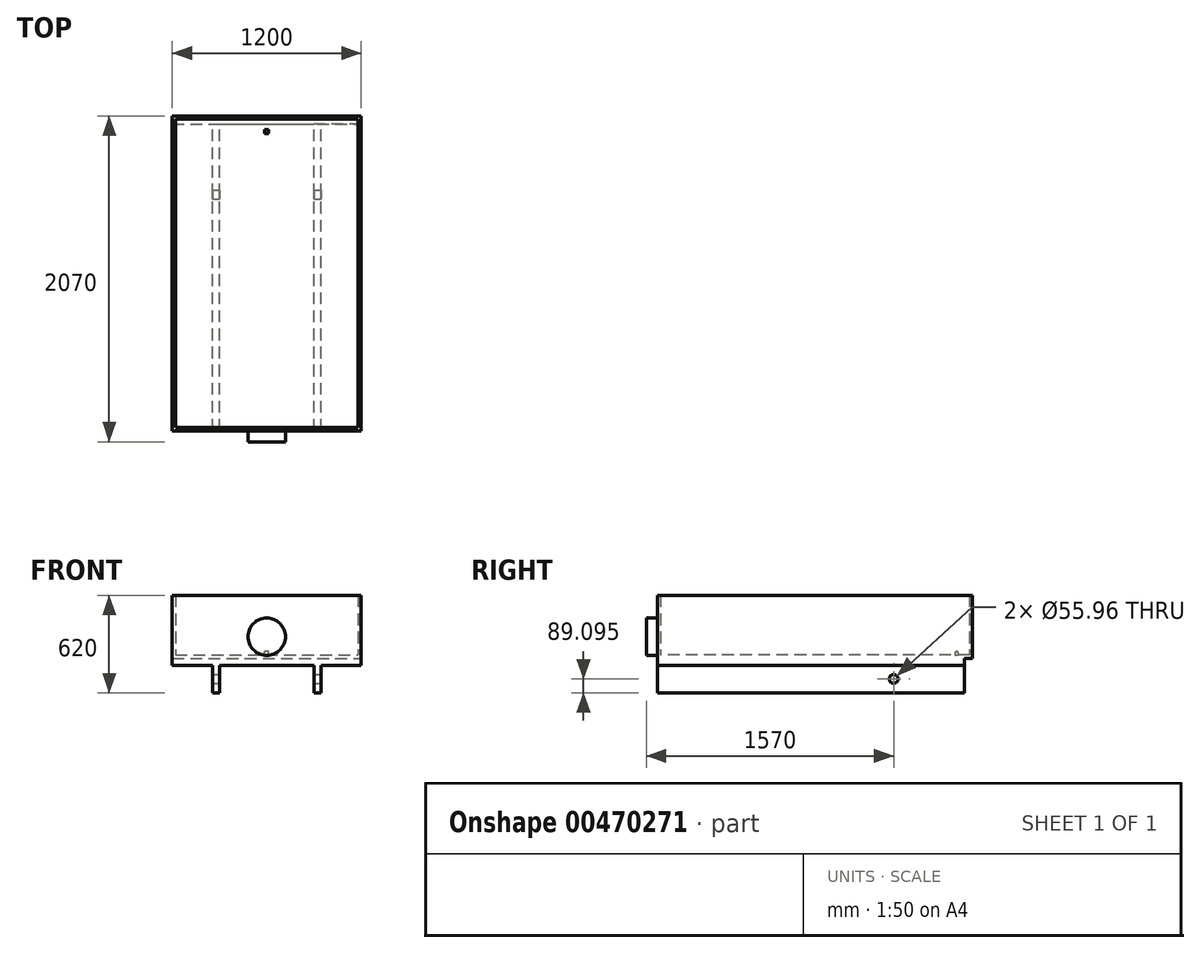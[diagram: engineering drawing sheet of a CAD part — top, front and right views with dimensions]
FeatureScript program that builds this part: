
annotation { "Feature Type Name" : "Feature", "Feature Type Description" : "" }
export const myFeature = defineFeature(function(context is Context, id is Id, definition is map)
    precondition{}
    {
        {
            var Q0;
            Q0=qCreatedBy(makeId("Top.planeOp"),FACE);
            var sketch = newSketch(context, id + "F0", { "sketchPlane" : qUnion([Q0])});
            skLineSegment(sketch, "E0.bottom", {"start": v(-600, 1000) * mm, "end": v(0, 1000) * mm});
            skLineSegment(sketch, "E0.top", {"start": v(-600, -1000) * mm, "end": v(0, -1000) * mm});
            skLineSegment(sketch, "E0.left", {"start": v(-600, 1000) * mm, "end": v(-600, -1000) * mm});
            skLineSegment(sketch, "E0.right", {"start": v(0, 1000) * mm, "end": v(0, -1000) * mm});
            skSolve(sketch);
        }
        {
            var Q0;
            Q0=makeQuery(id+"F0.imprint","IMPRINT",FACE,{"disambiguationData":[TD([[makeQuery(id+"F0.imprint","IMPRINT",EDGE,{"derivedFrom":sQuery(id+"F0.wireOp",EDGE,"E0.bottom")}),-1.0]])]});
            extrude(context, id + "F1", {"entities" : qUnion([Q0]), "depth" : 400 * mm});
        }
        {
            var Q0;
            Q0=makeQuery(id+"F1.opExtrude","CAP_FACE",FACE,{"disambiguationData":[OSD([sQuery(id+"F0.wireOp",EDGE,"E0.bottom"),sQuery(id+"F0.wireOp",EDGE,"E0.top"),sQuery(id+"F0.wireOp",EDGE,"E0.left"),sQuery(id+"F0.wireOp",EDGE,"E0.right")])],"isStart":false});
            var Q1;
            Q1=makeQuery(id+"F1.opExtrude","SWEPT_FACE",FACE,{"disambiguationData":[OSD([sQuery(id+"F0.wireOp",EDGE,"E0.right")])]});
            shell(context, id + "F2", {"entities" : qUnion([Q0, Q1]), "thickness" : 20 * mm});
        }
        {
            var Q0;
            {var subQ0=makeQuery(id+"F1.opExtrude","SWEPT_FACE",FACE,{"disambiguationData":[OSD([sQuery(id+"F0.wireOp",EDGE,"E0.top")])]});Q0=makeQuery(id+"F9.boolean.opBoolean","MERGE",FACE,{"derivedFrom":[subQ0,makeQuery(id+"F9.opPattern","COPY",FACE,{"derivedFrom":subQ0,"instanceName":"1"})]});}
            var sketch = newSketch(context, id + "F3", { "sketchPlane" : qUnion([Q0])});
            skCircle(sketch, "E1", {"center": v(0, 137.46) * mm, "radius": 119.04 * mm});
            skSolve(sketch);
        }
        {
            var Q0;
            Q0=makeQuery(id+"F3.imprint","IMPRINT",FACE,{"disambiguationData":[TD([[makeQuery(id+"F3.imprint","IMPRINT",EDGE,{"derivedFrom":sQuery(id+"F3.wireOp",EDGE,"E1")}),1.0]])]});
            extrude(context, id + "F4", {"entities" : qUnion([Q0]), "operationType" : NewBodyOperationType.ADD, "depth" : 70 * mm});
        }
        {
            var Q0;
            Q0=qCreatedBy(makeId("Right.planeOp"),FACE);
            var sketch = newSketch(context, id + "F5", { "sketchPlane" : qUnion([Q0])});
            skLineSegment(sketch, "E2", {"start": v(887.5, 30) * mm, "end": v(887.5, 0) * mm});
            skLineSegment(sketch, "E3", {"start": v(887.5, 30) * mm, "end": v(912.5, 30) * mm});
            skLineSegment(sketch, "E4", {"start": v(912.5, 0) * mm, "end": v(912.5, 30) * mm});
            skLineSegment(sketch, "E5", {"start": v(912.5, 0) * mm, "end": v(887.5, 0) * mm});
            skArc(sketch, "E6", {"start": v(912.5, 30) * mm, "mid": v(900, 42.5) * mm, "end": v(887.5, 30) * mm});
            skSolve(sketch);
        }
        {
            var Q0;
            Q0 = qSketchRegion(id + "F5", true);
            extrude(context, id + "F6", {"entities" : qUnion([Q0]), "operationType" : NewBodyOperationType.ADD, "endBound" : BoundingType.SYMMETRIC, "depth" : 25 * mm});
        }
        {
            var Q0;
            Q0=qCreatedBy(makeId("Front.planeOp"),FACE);
            var sketch = newSketch(context, id + "F7", { "sketchPlane" : qUnion([Q0])});
            skLineSegment(sketch, "E7.bottom", {"start": v(-345, 0) * mm, "end": v(-300, 0) * mm});
            skLineSegment(sketch, "E7.top", {"start": v(-345, -220) * mm, "end": v(-300, -220) * mm});
            skLineSegment(sketch, "E7.left", {"start": v(-345, 0) * mm, "end": v(-345, -220) * mm});
            skLineSegment(sketch, "E7.right", {"start": v(-300, 0) * mm, "end": v(-300, -220) * mm});
            skLineSegment(sketch, "E8.bottom", {"start": v(-600, -44.79) * mm, "end": v(0, -44.79) * mm});
            skLineSegment(sketch, "E8.top", {"start": v(-600, 0) * mm, "end": v(0, 0) * mm});
            skLineSegment(sketch, "E8.left", {"start": v(-600, -44.79) * mm, "end": v(-600, 0) * mm});
            skLineSegment(sketch, "E8.right", {"start": v(0, -44.79) * mm, "end": v(0, 0) * mm});
            skSolve(sketch);
        }
        {
            var Q0;
            {var subQ5=sQuery(id+"F7.wireOp",EDGE,"E8.right");Q0=makeQuery(id+"F7.imprint","IMPRINT",FACE,{"disambiguationData":[TD([[makeQuery(id+"F7.imprint","IMPRINT",EDGE,{"derivedFrom":subQ5}),1.0]])]});}
            var Q1;
            {var subQ0=sQuery(id+"F7.wireOp",EDGE,"E8.top");var subQ1=sQuery(id+"F7.wireOp",EDGE,"E7.left");var subQ2=makeQuery(id+"F7.imprint","INTERSECT",VERTEX,{"derivedFrom":[subQ1,subQ0]});Q1=makeQuery(id+"F7.imprint","IMPRINT",FACE,{"disambiguationData":[TD([[makeQuery(id+"F7.imprint","IMPRINT",EDGE,{"disambiguationData":[TD([[subQ2,-1.0]])],"derivedFrom":subQ1}),1.0]])]});}
            var Q2;
            {var subQ5=sQuery(id+"F7.wireOp",EDGE,"E8.left");Q2=makeQuery(id+"F7.imprint","IMPRINT",FACE,{"disambiguationData":[TD([[makeQuery(id+"F7.imprint","IMPRINT",EDGE,{"derivedFrom":subQ5}),-1.0]])]});}
            var Q3;
            {var subQ0=sQuery(id+"F7.wireOp",EDGE,"E7.top");Q3=makeQuery(id+"F7.imprint","IMPRINT",FACE,{"disambiguationData":[TD([[makeQuery(id+"F7.imprint","IMPRINT",EDGE,{"derivedFrom":subQ0}),1.0]])]});}
            extrude(context, id + "F8", {"entities" : qUnion([Q0, Q1, Q2, Q3]), "operationType" : NewBodyOperationType.ADD, "depth" : 1000 * mm, "hasSecondDirection" : true, "secondDirectionOppositeDirection" : true, "secondDirectionDepth" : 950 * mm});
        }
        {
            var Q0;
            Q0=makeQuery(id+"F1.opExtrude","SWEPT_BODY",BODY,{"disambiguationData":[OSD([sQuery(id+"F0.wireOp",EDGE,"E0.bottom"),sQuery(id+"F0.wireOp",EDGE,"E0.top"),sQuery(id+"F0.wireOp",EDGE,"E0.left"),sQuery(id+"F0.wireOp",EDGE,"E0.right")])]});
            var Q1;
            Q1=qCreatedBy(makeId("Right.planeOp"),FACE);
            mirror(context, id + "F9", {"operationType" : NewBodyOperationType.ADD, "entities" : qUnion([Q0]), "mirrorPlane" : qUnion([Q1])});
        }
        {
            var Q0;
            Q0=qCreatedBy(makeId("Right.planeOp"),FACE);
            var sketch = newSketch(context, id + "F10", { "sketchPlane" : qUnion([Q0])});
            skCircle(sketch, "E9", {"center": v(500, -130.9) * mm, "radius": 27.98 * mm});
            skSolve(sketch);
        }
        {
            var Q0;
            Q0 = qSketchRegion(id + "F10", true);
            extrude(context, id + "F11", {"entities" : qUnion([Q0]), "operationType" : NewBodyOperationType.REMOVE, "endBound" : BoundingType.THROUGH_ALL, "oppositeDirection" : true, "depth" : 25 * mm, "hasSecondDirection" : true, "secondDirectionBound" : SecondDirectionBoundingType.THROUGH_ALL, "secondDirectionOppositeDirection" : false, "secondDirectionDepth" : 25 * mm});
        }
    });
